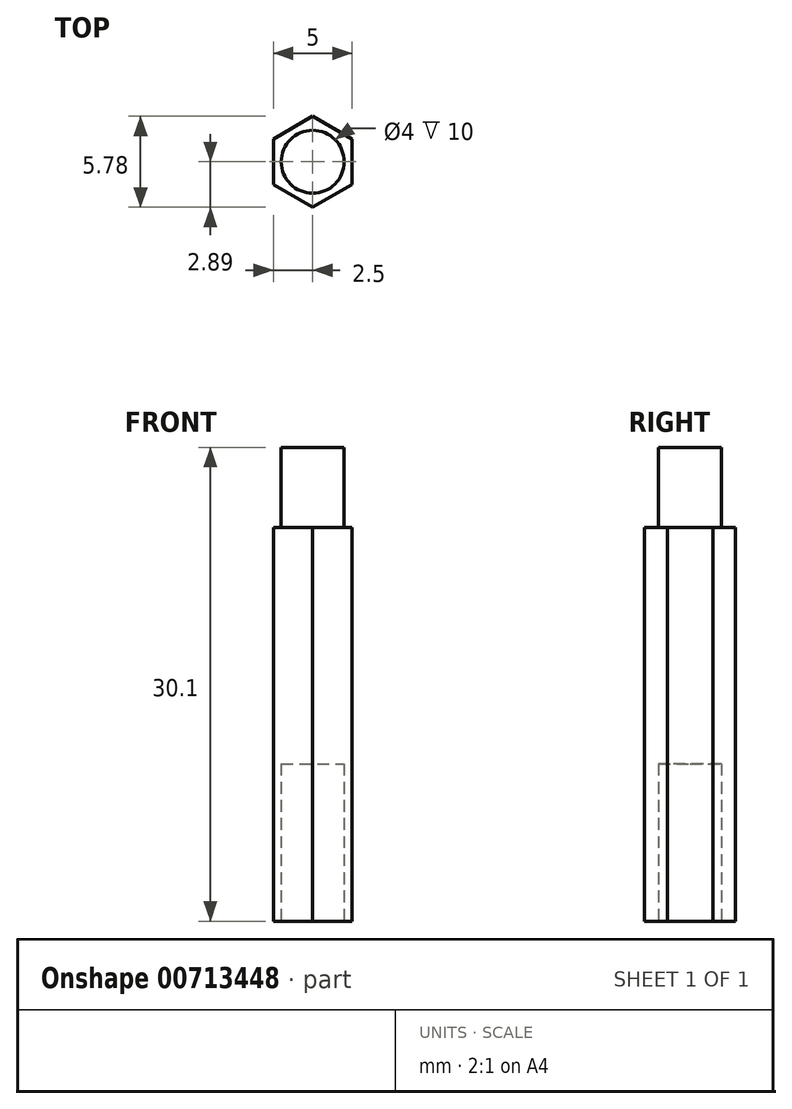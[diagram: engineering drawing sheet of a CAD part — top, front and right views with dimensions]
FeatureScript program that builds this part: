
annotation { "Feature Type Name" : "Feature", "Feature Type Description" : "" }
export const myFeature = defineFeature(function(context is Context, id is Id, definition is map)
    precondition{}
    {
        {
            var Q0;
            Q0=qCreatedBy(makeId("Top.planeOp"),FACE);
            var sketch = newSketch(context, id + "F0", { "sketchPlane" : qUnion([Q0])});
            skCircle(sketch, "E0.cCircle", {"center": v(0, 0) * mm, "radius": 2.5 * mm, "construction": true});
            skLineSegment(sketch, "E0.0", {"start": v(0, 2.89) * mm, "end": v(2.5, 1.44) * mm});
            skLineSegment(sketch, "E0.1", {"start": v(2.5, 1.44) * mm, "end": v(2.5, -1.44) * mm});
            skLineSegment(sketch, "E0.2", {"start": v(2.5, -1.44) * mm, "end": v(0, -2.89) * mm});
            skLineSegment(sketch, "E0.3", {"start": v(0, -2.89) * mm, "end": v(-2.5, -1.44) * mm});
            skLineSegment(sketch, "E0.4", {"start": v(-2.5, -1.44) * mm, "end": v(-2.5, 1.44) * mm});
            skLineSegment(sketch, "E0.5", {"start": v(-2.5, 1.44) * mm, "end": v(0, 2.89) * mm});
            skPoint(sketch, "E0.0.midPoint", {"position": v(1.25, 2.17) * mm});
            skSolve(sketch);
        }
        {
            var Q0;
            Q0 = qSketchRegion(id + "F0", true);
            extrude(context, id + "F1", {"entities" : qUnion([Q0]), "depth" : 25 * mm, "offsetDistance" : 25 * mm});
        }
        {
            var Q0;
            Q0=makeQuery(id+"F1.opExtrude","CAP_FACE",FACE,{"disambiguationData":[OSD([sQuery(id+"F0.wireOp",EDGE,"E0.0"),sQuery(id+"F0.wireOp",EDGE,"E0.1"),sQuery(id+"F0.wireOp",EDGE,"E0.2"),sQuery(id+"F0.wireOp",EDGE,"E0.3"),sQuery(id+"F0.wireOp",EDGE,"E0.4"),sQuery(id+"F0.wireOp",EDGE,"E0.5")])],"isStart":false});
            var sketch = newSketch(context, id + "F2", { "sketchPlane" : qUnion([Q0])});
            skCircle(sketch, "E1", {"center": v(0, 0) * mm, "radius": 2 * mm});
            skSolve(sketch);
        }
        {
            var Q0;
            Q0 = qSketchRegion(id + "F2", true);
            extrude(context, id + "F3", {"entities" : qUnion([Q0]), "operationType" : NewBodyOperationType.ADD, "depth" : 5.1 * mm, "offsetDistance" : 25 * mm});
        }
        {
            var Q0;
            Q0=makeQuery(id+"F1.opExtrude","CAP_FACE",FACE,{"disambiguationData":[OSD([sQuery(id+"F0.wireOp",EDGE,"E0.0"),sQuery(id+"F0.wireOp",EDGE,"E0.1"),sQuery(id+"F0.wireOp",EDGE,"E0.2"),sQuery(id+"F0.wireOp",EDGE,"E0.3"),sQuery(id+"F0.wireOp",EDGE,"E0.4"),sQuery(id+"F0.wireOp",EDGE,"E0.5")])],"isStart":true});
            var sketch = newSketch(context, id + "F4", { "sketchPlane" : qUnion([Q0])});
            skCircle(sketch, "E2", {"center": v(0, 0) * mm, "radius": 2 * mm});
            skSolve(sketch);
        }
        {
            var Q0;
            Q0 = qSketchRegion(id + "F4", true);
            extrude(context, id + "F5", {"entities" : qUnion([Q0]), "operationType" : NewBodyOperationType.REMOVE, "oppositeDirection" : true, "depth" : 10 * mm, "offsetDistance" : 25 * mm});
        }
    });
